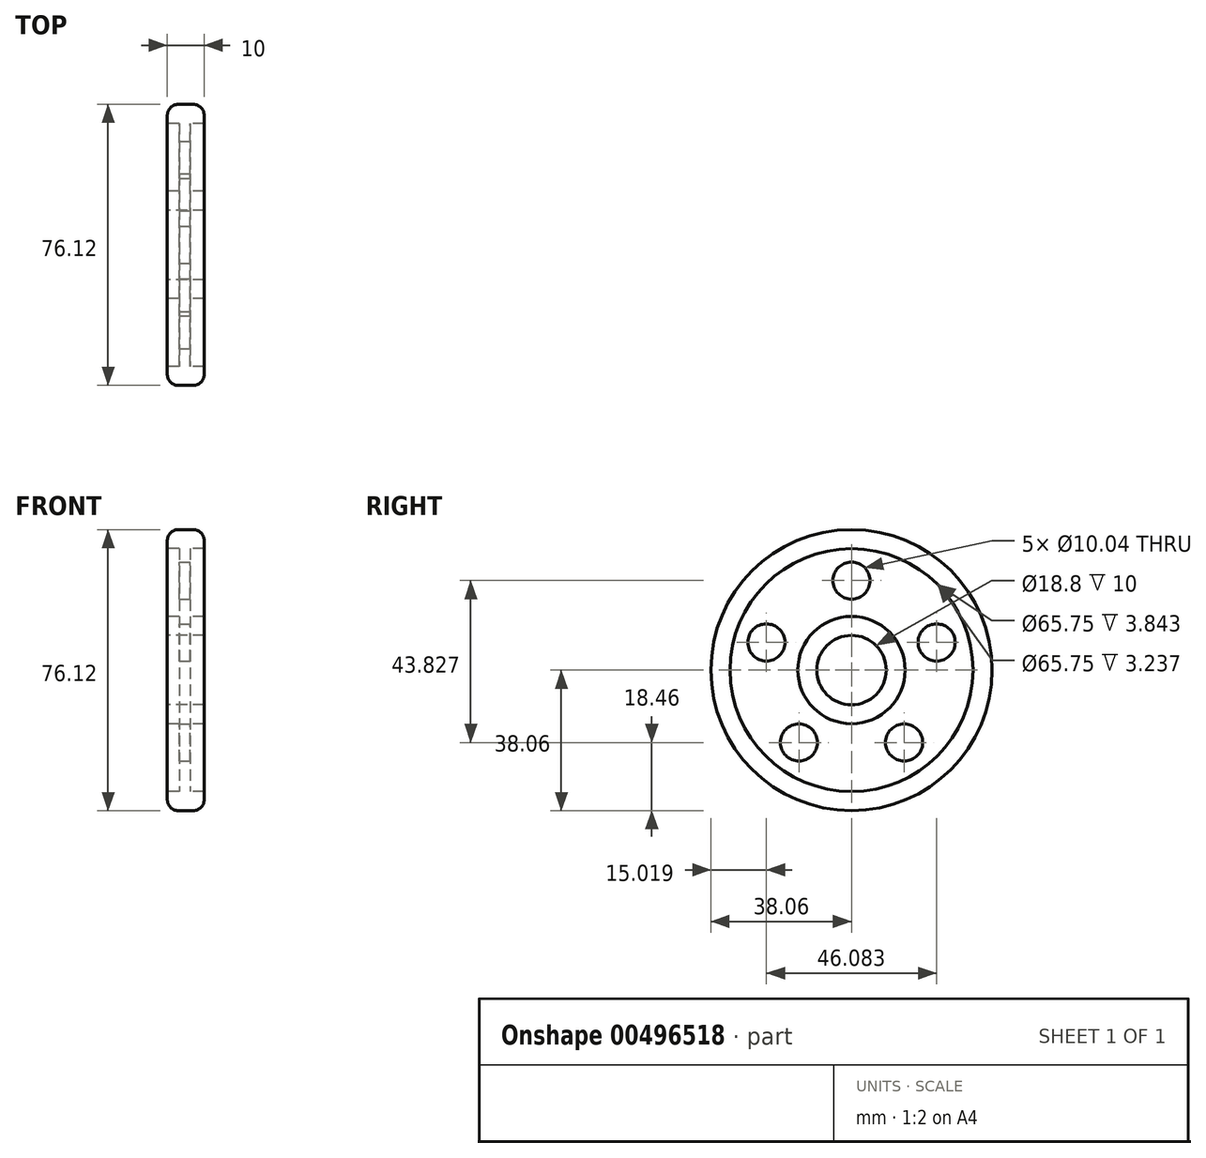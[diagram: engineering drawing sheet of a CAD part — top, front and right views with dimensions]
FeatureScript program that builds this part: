
annotation { "Feature Type Name" : "Feature", "Feature Type Description" : "" }
export const myFeature = defineFeature(function(context is Context, id is Id, definition is map)
    precondition{}
    {
        {
            var Q0;
            Q0=qCreatedBy(makeId("Front.planeOp"),FACE);
            var sketch = newSketch(context, id + "F0", { "sketchPlane" : qUnion([Q0])});
            skLineSegment(sketch, "E0", {"start": v(0, 9.4) * mm, "end": v(10, 9.4) * mm});
            skLineSegment(sketch, "E1", {"start": v(10, 9.4) * mm, "end": v(10, 14.53) * mm});
            skLineSegment(sketch, "E2", {"start": v(10, 14.53) * mm, "end": v(6.16, 14.53) * mm});
            skLineSegment(sketch, "E3", {"start": v(6.16, 14.53) * mm, "end": v(6.16, 32.88) * mm});
            skLineSegment(sketch, "E4", {"start": v(6.16, 32.88) * mm, "end": v(10, 32.88) * mm});
            skLineSegment(sketch, "E5", {"start": v(10, 32.88) * mm, "end": v(10, 38.06) * mm});
            skLineSegment(sketch, "E6", {"start": v(10, 38.06) * mm, "end": v(0, 38.06) * mm});
            skLineSegment(sketch, "E7", {"start": v(0, 38.06) * mm, "end": v(0, 32.88) * mm});
            skLineSegment(sketch, "E8", {"start": v(0, 32.88) * mm, "end": v(3.24, 32.88) * mm});
            skLineSegment(sketch, "E9", {"start": v(3.24, 32.88) * mm, "end": v(3.24, 14.53) * mm});
            skLineSegment(sketch, "E10", {"start": v(3.24, 14.53) * mm, "end": v(0, 14.53) * mm});
            skLineSegment(sketch, "E11", {"start": v(0, 14.53) * mm, "end": v(0, 9.4) * mm});
            skLineSegment(sketch, "E12", {"start": v(0, 0) * mm, "end": v(10, 0) * mm});
            skSolve(sketch);
        }
        {
            var Q0;
            Q0 = qSketchRegion(id + "F0", true);
            var Q1;
            Q1=sQuery(id+"F0.wireOp",EDGE,"E12");
            revolve(context, id + "F1", {"entities" : qUnion([Q0]), "axis" : qUnion([Q1]), "revolveType" : RevolveType.FULL});
        }
        {
            var Q0;
            Q0=makeQuery(id+"F1.opRevolve","SWEPT_FACE",FACE,{"disambiguationData":[OSD([sQuery(id+"F0.wireOp",EDGE,"E3")])]});
            var sketch = newSketch(context, id + "F2", { "sketchPlane" : qUnion([Q0])});
            skCircle(sketch, "E13", {"center": v(0, 24.23) * mm, "radius": 5.02 * mm});
            skCircle(sketch, "E14.1.0", {"center": v(-23.04, 7.49) * mm, "radius": 5.02 * mm});
            skCircle(sketch, "E14.2.0", {"center": v(-14.24, -19.6) * mm, "radius": 5.02 * mm});
            skCircle(sketch, "E14.3.0", {"center": v(14.24, -19.6) * mm, "radius": 5.02 * mm});
            skCircle(sketch, "E14.4.0", {"center": v(23.04, 7.49) * mm, "radius": 5.02 * mm});
            skPoint(sketch, "E14.center", {"position": v(0, 0) * mm});
            skSolve(sketch);
        }
        {
            var Q0;
            Q0=makeQuery(id+"F2.imprint","IMPRINT",FACE,{"disambiguationData":[TD([[makeQuery(id+"F2.imprint","IMPRINT",EDGE,{"derivedFrom":sQuery(id+"F2.wireOp",EDGE,"E14.1.0")}),1.0]])]});
            var Q1;
            Q1=makeQuery(id+"F2.imprint","IMPRINT",FACE,{"disambiguationData":[TD([[makeQuery(id+"F2.imprint","IMPRINT",EDGE,{"derivedFrom":sQuery(id+"F2.wireOp",EDGE,"E13")}),1.0]])]});
            var Q2;
            Q2=makeQuery(id+"F2.imprint","IMPRINT",FACE,{"disambiguationData":[TD([[makeQuery(id+"F2.imprint","IMPRINT",EDGE,{"derivedFrom":sQuery(id+"F2.wireOp",EDGE,"E14.4.0")}),1.0]])]});
            var Q3;
            Q3=makeQuery(id+"F2.imprint","IMPRINT",FACE,{"disambiguationData":[TD([[makeQuery(id+"F2.imprint","IMPRINT",EDGE,{"derivedFrom":sQuery(id+"F2.wireOp",EDGE,"E14.3.0")}),1.0]])]});
            var Q4;
            Q4=makeQuery(id+"F2.imprint","IMPRINT",FACE,{"disambiguationData":[TD([[makeQuery(id+"F2.imprint","IMPRINT",EDGE,{"derivedFrom":sQuery(id+"F2.wireOp",EDGE,"E14.2.0")}),1.0]])]});
            extrude(context, id + "F3", {"entities" : qUnion([Q0, Q1, Q2, Q3, Q4]), "operationType" : NewBodyOperationType.REMOVE, "oppositeDirection" : true, "depth" : 25 * mm});
        }
        {
            var Q0;
            Q0=makeQuery(id+"F1.opRevolve","SWEPT_EDGE",EDGE,{"disambiguationData":[OSD([sQuery(id+"F0.wireOp",EDGE,"E6"),sQuery(id+"F0.wireOp",EDGE,"E7")])]});
            var Q1;
            Q1=makeQuery(id+"F1.opRevolve","SWEPT_EDGE",EDGE,{"disambiguationData":[OSD([sQuery(id+"F0.wireOp",EDGE,"E5"),sQuery(id+"F0.wireOp",EDGE,"E6")])]});
            fillet(context, id + "F4", {"entities" : qUnion([Q0, Q1]), "radius" : 3 * mm, "tangentPropagation" : true, "allowEdgeOverflow" : false});
        }
    });
